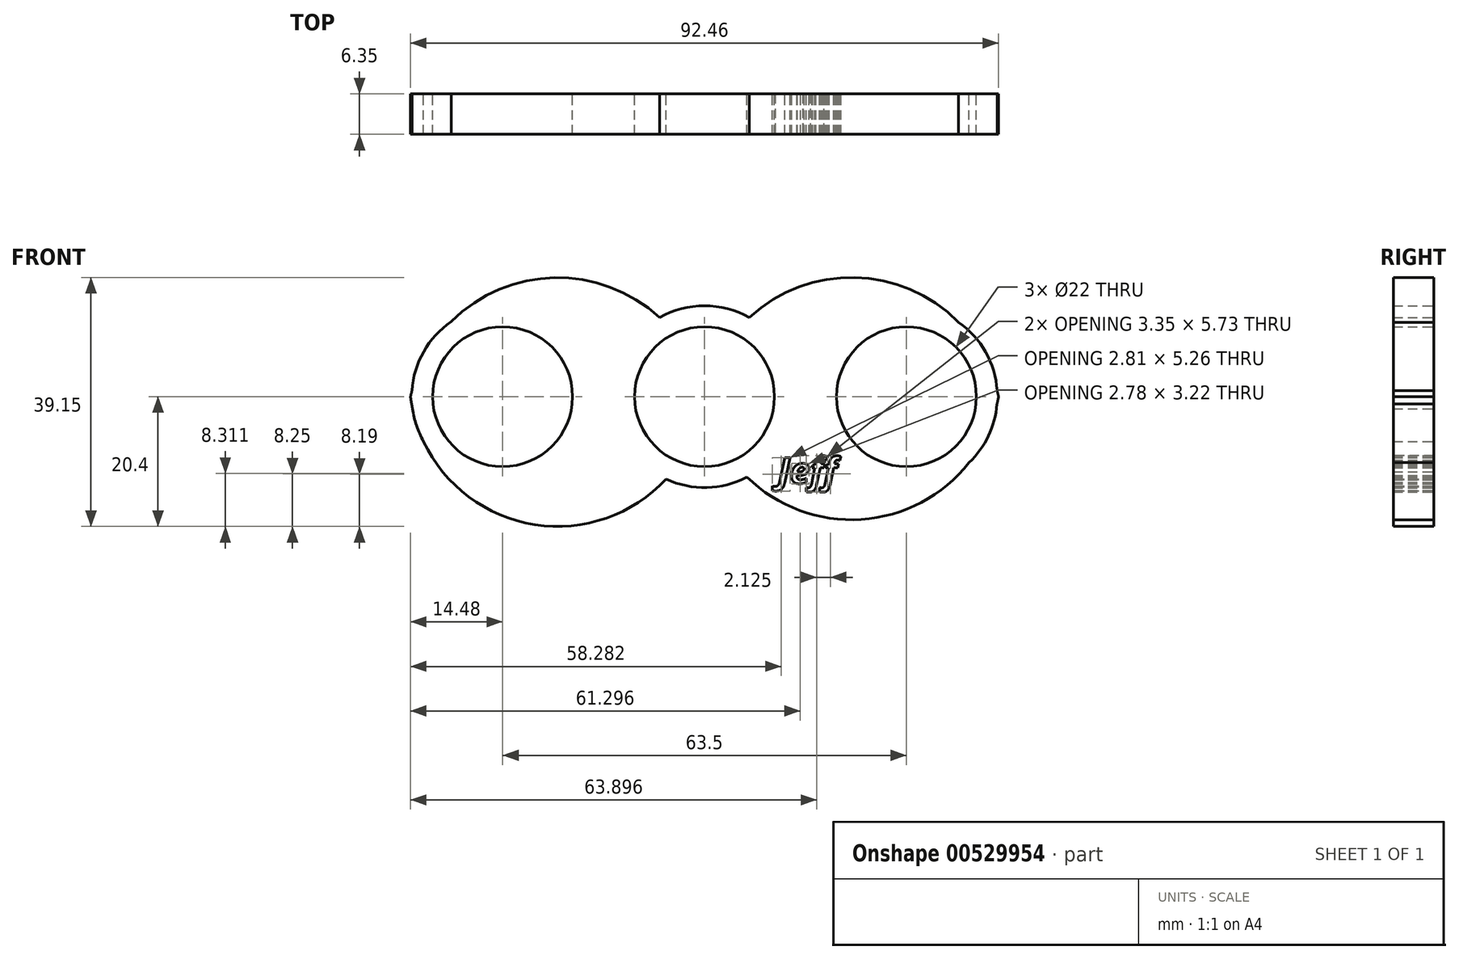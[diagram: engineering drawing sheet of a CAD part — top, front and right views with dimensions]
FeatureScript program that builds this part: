
annotation { "Feature Type Name" : "Feature", "Feature Type Description" : "" }
export const myFeature = defineFeature(function(context is Context, id is Id, definition is map)
    precondition{}
    {
        {
            var Q0;
            Q0=qCreatedBy(makeId("Front.planeOp"),FACE);
            var sketch = newSketch(context, id + "F0", { "sketchPlane" : qUnion([Q0])});
            skCircle(sketch, "E0", {"center": v(0, 0) * mm, "radius": 14.29 * mm});
            skCircle(sketch, "E1", {"center": v(0, 0) * mm, "radius": 11 * mm});
            skCircle(sketch, "E2", {"center": v(-31.75, 0) * mm, "radius": 14.29 * mm});
            skCircle(sketch, "E3", {"center": v(-31.75, 0) * mm, "radius": 11 * mm});
            skCircle(sketch, "E4.1.0", {"center": v(31.75, 0) * mm, "radius": 14.29 * mm});
            skCircle(sketch, "E4.1.1", {"center": v(31.75, 0) * mm, "radius": 11 * mm});
            skSolve(sketch);
        }
        {
            var Q0;
            Q0=qCreatedBy(makeId("Front.planeOp"),FACE);
            var sketch = newSketch(context, id + "F1", { "sketchPlane" : qUnion([Q0])});
            skArc(sketch, "E5", {"start": v(0, 0) * mm, "mid": v(-23.11, 18.71) * mm, "end": v(-46.23, 0) * mm});
            skArc(sketch, "E6", {"start": v(46.23, 0) * mm, "mid": v(23.11, 18.75) * mm, "end": v(0, 0) * mm});
            skArc(sketch, "E7", {"start": v(-46.23, 0) * mm, "mid": v(-23.11, -20.4) * mm, "end": v(0, 0) * mm});
            skArc(sketch, "E8", {"start": v(0, 0) * mm, "mid": v(23.11, -19.35) * mm, "end": v(46.23, 0) * mm});
            skSolve(sketch);
        }
        {
            var Q0;
            Q0=qCreatedBy(makeId("Front.planeOp"),FACE);
            var sketch = newSketch(context, id + "F2", { "sketchPlane" : qUnion([Q0])});
            skCircle(sketch, "E9.0", {"center": v(-31.75, 0) * mm, "radius": 14.29 * mm});
            skCircle(sketch, "E10.0", {"center": v(-31.75, 0) * mm, "radius": 11 * mm});
            skArc(sketch, "E11.0", {"start": v(0, 0) * mm, "mid": v(-23.11, 18.71) * mm, "end": v(-46.23, 0) * mm});
            skArc(sketch, "E12.0", {"start": v(-46.23, 0) * mm, "mid": v(-23.11, -20.4) * mm, "end": v(0, 0) * mm});
            skCircle(sketch, "E13.0", {"center": v(0, 0) * mm, "radius": 11 * mm});
            skCircle(sketch, "E14.0", {"center": v(0, 0) * mm, "radius": 14.29 * mm});
            skArc(sketch, "E15.0", {"start": v(46.23, 0) * mm, "mid": v(23.11, 18.75) * mm, "end": v(0, 0) * mm});
            skArc(sketch, "E16.0", {"start": v(0, 0) * mm, "mid": v(23.11, -19.35) * mm, "end": v(46.23, 0) * mm});
            skCircle(sketch, "E17.0", {"center": v(31.75, 0) * mm, "radius": 14.29 * mm});
            skCircle(sketch, "E18.0", {"center": v(31.75, 0) * mm, "radius": 11 * mm});
            skSolve(sketch);
        }
        {
            var Q0;
            Q0 = qSketchRegion(id + "F2", true);
            extrude(context, id + "F3", {"entities" : qUnion([Q0]), "depth" : 6.35 * mm, "offsetDistance" : 25.4 * mm});
        }
        {
            var Q0;
            Q0=qCreatedBy(makeId("Front.planeOp"),FACE);
            var sketch = newSketch(context, id + "F4", { "sketchPlane" : qUnion([Q0])});
            skText(sketch, "E19", { "text": "\nJeff\n", "fontName": "OpenSans-BoldItalic.ttf"});
            const initialGuessF4  = {"E19": [0.01154, -0.0059, 1, 0, 0.0041]};
            skSetInitialGuess(sketch, initialGuessF4);
            skSolve(sketch);
        }
        {
            var Q0;
            Q0 = qSketchRegion(id + "F4", true);
            extrude(context, id + "F5", {"entities" : qUnion([Q0]), "operationType" : NewBodyOperationType.REMOVE, "endBound" : BoundingType.THROUGH_ALL, "depth" : 22.86 * mm, "offsetDistance" : 25.4 * mm});
        }
    });
